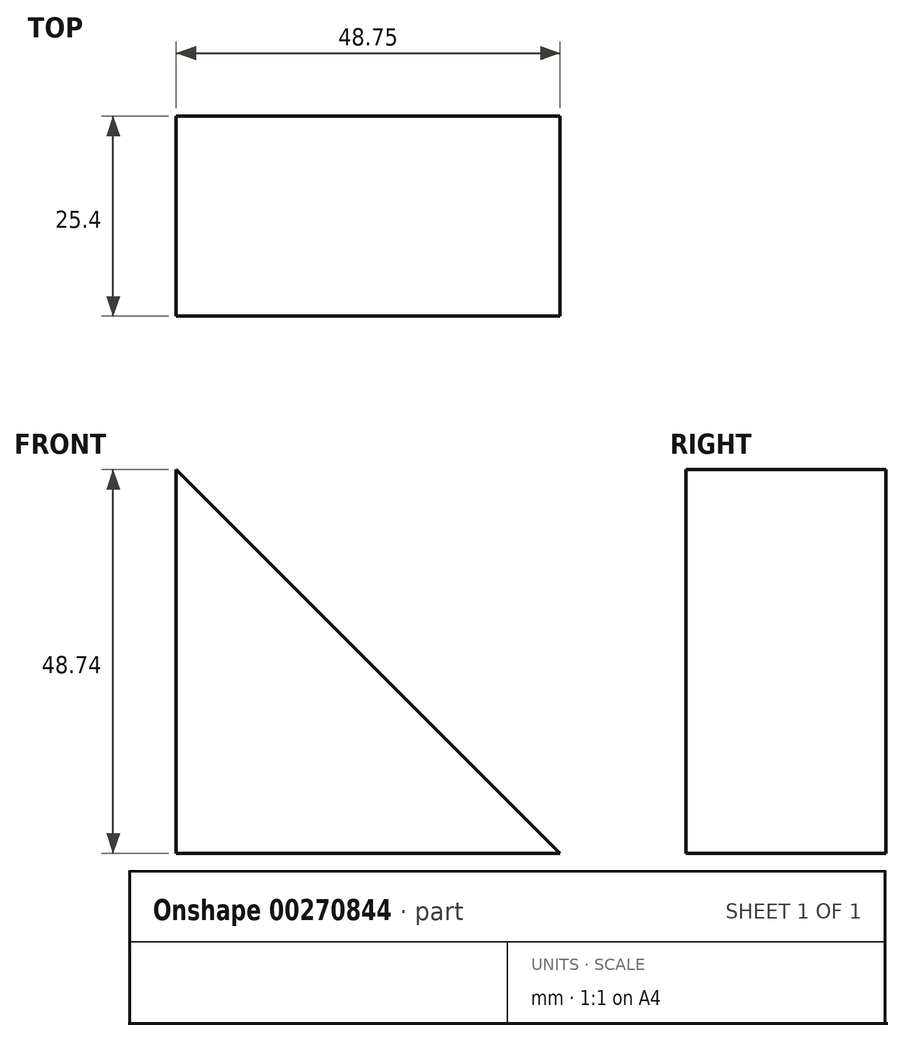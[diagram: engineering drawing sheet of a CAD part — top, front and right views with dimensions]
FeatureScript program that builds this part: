
annotation { "Feature Type Name" : "Feature", "Feature Type Description" : "" }
export const myFeature = defineFeature(function(context is Context, id is Id, definition is map)
    precondition{}
    {
        {
            var Q0;
            Q0=qCreatedBy(makeId("Front.planeOp"),FACE);
            var sketch = newSketch(context, id + "F0", { "sketchPlane" : qUnion([Q0])});
            skLineSegment(sketch, "E0", {"start": v(0, 0) * mm, "end": v(-48.75, 0) * mm});
            skLineSegment(sketch, "E1", {"start": v(-48.75, 0) * mm, "end": v(-48.75, 48.74) * mm});
            skLineSegment(sketch, "E2", {"start": v(-48.75, 48.74) * mm, "end": v(0, 0) * mm});
            skSolve(sketch);
        }
        {
            var Q0;
            Q0 = qSketchRegion(id + "F0", true);
            extrude(context, id + "F1", {"entities" : qUnion([Q0]), "depth" : 25.4 * mm});
        }
    });
